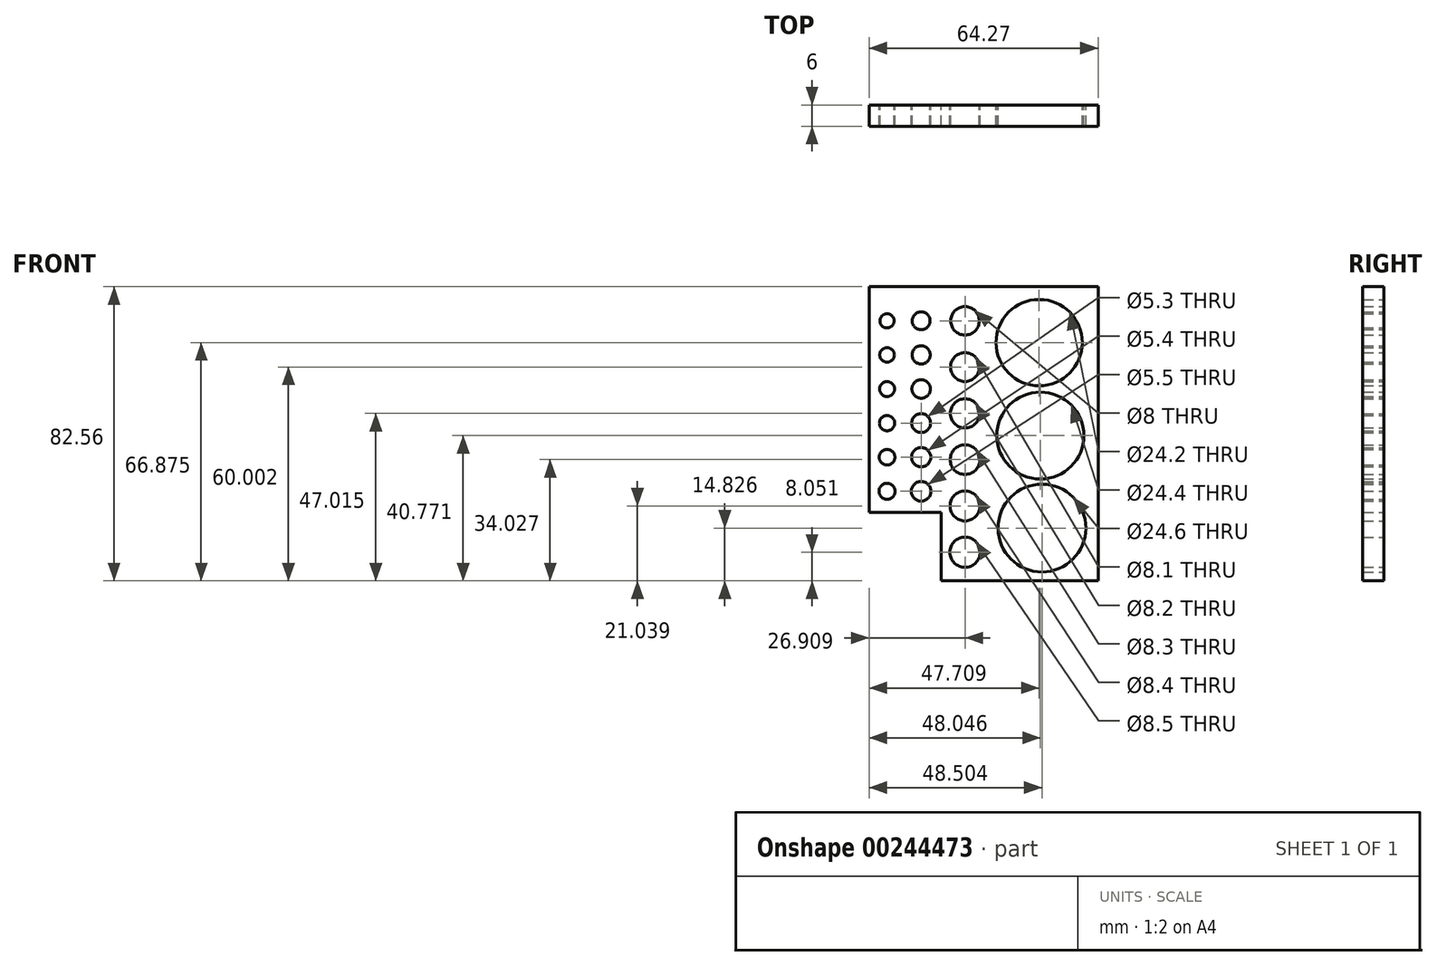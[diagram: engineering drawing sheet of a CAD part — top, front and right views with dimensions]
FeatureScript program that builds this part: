
annotation { "Feature Type Name" : "Feature", "Feature Type Description" : "" }
export const myFeature = defineFeature(function(context is Context, id is Id, definition is map)
    precondition{}
    {
        {
            var Q0;
            Q0=qCreatedBy(makeId("Front.planeOp"),FACE);
            var sketch = newSketch(context, id + "F0", { "sketchPlane" : qUnion([Q0])});
            skLineSegment(sketch, "E0", {"start": v(0, 0) * mm, "end": v(-54.69, 0) * mm});
            skLineSegment(sketch, "E1", {"start": v(-54.69, 0) * mm, "end": v(-54.69, -9.57) * mm, "construction": true});
            skCircle(sketch, "E2", {"center": v(-54.69, -9.57) * mm, "radius": 2 * mm});
            skLineSegment(sketch, "E3", {"start": v(-54.69, -9.57) * mm, "end": v(-54.69, -19.14) * mm, "construction": true});
            skLineSegment(sketch, "E4", {"start": v(-54.69, -19.14) * mm, "end": v(-54.69, -28.7) * mm, "construction": true});
            skLineSegment(sketch, "E5", {"start": v(-54.69, -28.7) * mm, "end": v(-54.69, -38.28) * mm, "construction": true});
            skLineSegment(sketch, "E6", {"start": v(-54.69, -38.28) * mm, "end": v(-54.69, -47.85) * mm, "construction": true});
            skLineSegment(sketch, "E7", {"start": v(-54.69, -47.85) * mm, "end": v(-54.69, -57.42) * mm, "construction": true});
            skCircle(sketch, "E8", {"center": v(-54.69, -19.14) * mm, "radius": 2.05 * mm});
            skCircle(sketch, "E9", {"center": v(-54.69, -28.7) * mm, "radius": 2.1 * mm});
            skCircle(sketch, "E10", {"center": v(-54.69, -38.28) * mm, "radius": 2.15 * mm});
            skCircle(sketch, "E11", {"center": v(-54.69, -47.85) * mm, "radius": 2.2 * mm});
            skCircle(sketch, "E12", {"center": v(-54.69, -57.42) * mm, "radius": 2.25 * mm});
            skLineSegment(sketch, "E13", {"start": v(-45.12, 0) * mm, "end": v(-45.12, -9.57) * mm, "construction": true});
            skCircle(sketch, "E14", {"center": v(-45.12, -9.57) * mm, "radius": 2.5 * mm});
            skLineSegment(sketch, "E15", {"start": v(-45.12, -9.57) * mm, "end": v(-45.12, -19.14) * mm, "construction": true});
            skLineSegment(sketch, "E16", {"start": v(-45.12, -19.14) * mm, "end": v(-45.12, -28.7) * mm, "construction": true});
            skLineSegment(sketch, "E17", {"start": v(-45.12, -28.7) * mm, "end": v(-45.12, -38.28) * mm, "construction": true});
            skLineSegment(sketch, "E18", {"start": v(-45.12, -38.28) * mm, "end": v(-45.12, -47.85) * mm, "construction": true});
            skLineSegment(sketch, "E19", {"start": v(-45.12, -47.85) * mm, "end": v(-45.12, -57.42) * mm, "construction": true});
            skCircle(sketch, "E20", {"center": v(-45.12, -19.14) * mm, "radius": 2.55 * mm});
            skCircle(sketch, "E21", {"center": v(-45.12, -28.7) * mm, "radius": 2.6 * mm});
            skCircle(sketch, "E22", {"center": v(-45.12, -38.28) * mm, "radius": 2.65 * mm});
            skCircle(sketch, "E23", {"center": v(-45.12, -47.85) * mm, "radius": 2.7 * mm});
            skCircle(sketch, "E24", {"center": v(-45.12, -57.42) * mm, "radius": 2.75 * mm});
            skPoint(sketch, "E25", {"position": v(-45.12, 0) * mm});
            skPoint(sketch, "E26", {"position": v(-32.81, 0) * mm});
            skLineSegment(sketch, "E27", {"start": v(-32.81, 0) * mm, "end": v(-32.81, -9.57) * mm, "construction": true});
            skCircle(sketch, "E28", {"center": v(-32.81, -9.57) * mm, "radius": 4 * mm});
            skLineSegment(sketch, "E29", {"start": v(-32.81, -9.57) * mm, "end": v(-32.81, -22.56) * mm});
            skLineSegment(sketch, "E30", {"start": v(-32.81, -22.56) * mm, "end": v(-32.81, -35.55) * mm});
            skLineSegment(sketch, "E31", {"start": v(-32.81, -35.55) * mm, "end": v(-32.81, -48.53) * mm});
            skLineSegment(sketch, "E32", {"start": v(-32.81, -48.53) * mm, "end": v(-32.81, -61.52) * mm});
            skLineSegment(sketch, "E33", {"start": v(-32.81, -61.52) * mm, "end": v(-32.81, -74.5) * mm});
            skCircle(sketch, "E34", {"center": v(-32.81, -22.56) * mm, "radius": 4.05 * mm});
            skCircle(sketch, "E35", {"center": v(-32.81, -35.55) * mm, "radius": 4.1 * mm});
            skCircle(sketch, "E36", {"center": v(-32.81, -48.53) * mm, "radius": 4.15 * mm});
            skCircle(sketch, "E37", {"center": v(-32.81, -61.52) * mm, "radius": 4.2 * mm});
            skCircle(sketch, "E38", {"center": v(-32.81, -74.5) * mm, "radius": 4.25 * mm});
            skCircle(sketch, "E39", {"center": v(-12.01, -15.68) * mm, "radius": 12.1 * mm});
            skCircle(sketch, "E40", {"center": v(-11.67, -41.79) * mm, "radius": 12.2 * mm});
            skCircle(sketch, "E41", {"center": v(-11.22, -67.73) * mm, "radius": 12.3 * mm});
            skLineSegment(sketch, "E42", {"start": v(-54.69, 0) * mm, "end": v(-59.72, 0) * mm});
            skLineSegment(sketch, "E43", {"start": v(-59.72, 0) * mm, "end": v(-59.72, -63.38) * mm});
            skLineSegment(sketch, "E44", {"start": v(-59.72, -63.38) * mm, "end": v(-39.55, -63.38) * mm});
            skLineSegment(sketch, "E45", {"start": v(-39.55, -63.38) * mm, "end": v(-39.55, -82.56) * mm});
            skLineSegment(sketch, "E46", {"start": v(-39.55, -82.56) * mm, "end": v(4.55, -82.56) * mm});
            skLineSegment(sketch, "E47", {"start": v(4.55, -82.56) * mm, "end": v(4.55, 0) * mm});
            skLineSegment(sketch, "E48", {"start": v(4.55, 0) * mm, "end": v(0, 0) * mm});
            skSolve(sketch);
        }
        {
            var Q0;
            Q0=makeQuery(id+"F0.imprint","IMPRINT",FACE,{"disambiguationData":[TD([[makeQuery(id+"F0.imprint","IMPRINT",EDGE,{"derivedFrom":sQuery(id+"F0.wireOp",EDGE,"E0")}),1.0]])]});
            extrude(context, id + "F1", {"entities" : qUnion([Q0]), "depth" : 6 * mm});
        }
    });
